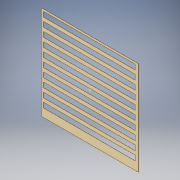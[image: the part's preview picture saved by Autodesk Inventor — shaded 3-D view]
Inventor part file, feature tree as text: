
AUTODESK INVENTOR PART (.ipt)
format: ipt  version: 2018 (Build 220112000, 112)  size: 148,992 bytes
history: native  units: in
note: dims shown in document units (in); Inventor stores cm internally (conversion verified against a paired STEP export)
features: sketch x2, extrude x2
ambient origin geometry x8: Origin, YZ Plane, XZ Plane, XY Plane, X Axis, Y Axis, Z Axis, Center Point
bodies: Solid1 (feature_tree)
feature tree (4):
  sketch  "Sketch1"  dims[d0=730.0in d1=710.0in]
  extrude  "Extrusion1"  Depth=710.0in
  extrude  "Extrusion2"  Depth=1.0in TaperAngle=0.0deg
  sketch  "Sketch3"  dims[d2=240.0in d3=1.0in d4=0.0in d5=3.937in d7=66.0in d8=0.3937in d10=1.0in d12=1.0in d13=0.0in]
